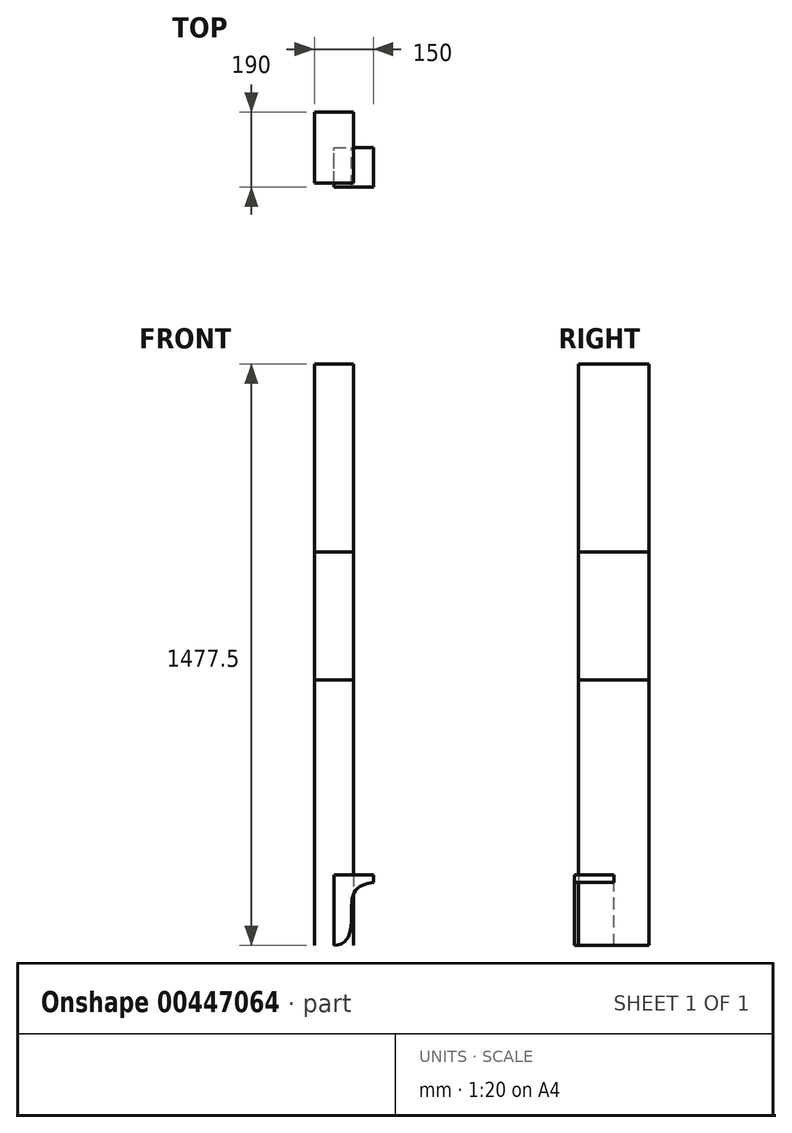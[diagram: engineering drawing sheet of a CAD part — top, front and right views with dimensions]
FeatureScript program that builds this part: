
annotation { "Feature Type Name" : "Feature", "Feature Type Description" : "" }
export const myFeature = defineFeature(function(context is Context, id is Id, definition is map)
    precondition{}
    {
        {
            var Q0;
            Q0=qCreatedBy(makeId("Top.planeOp"),FACE);
            var sketch = newSketch(context, id + "F0", { "sketchPlane" : qUnion([Q0])});
            skLineSegment(sketch, "E0.bottom", {"start": v(50, -90) * mm, "end": v(-50, -90) * mm});
            skLineSegment(sketch, "E0.top", {"start": v(50, 90) * mm, "end": v(-50, 90) * mm});
            skLineSegment(sketch, "E0.left", {"start": v(50, -90) * mm, "end": v(50, 90) * mm});
            skLineSegment(sketch, "E0.right", {"start": v(-50, -90) * mm, "end": v(-50, 90) * mm});
            skPoint(sketch, "E0.middle", {"position": v(0, 0) * mm});
            skSolve(sketch);
        }
        {
            var Q0;
            Q0=makeQuery(id+"F0.imprint","IMPRINT",FACE,{"disambiguationData":[TD([[makeQuery(id+"F0.imprint","IMPRINT",EDGE,{"derivedFrom":sQuery(id+"F0.wireOp",EDGE,"E0.bottom")}),-1.0]])]});
            extrude(context, id + "F1", {"entities" : qUnion([Q0]), "depth" : 1000 * mm, "offsetDistance" : 25 * mm});
        }
        {
            var Q0;
            Q0=makeQuery(id+"F0.imprint","IMPRINT",FACE,{"disambiguationData":[TD([[makeQuery(id+"F0.imprint","IMPRINT",EDGE,{"derivedFrom":sQuery(id+"F0.wireOp",EDGE,"E0.bottom")}),-1.0]])]});
            extrude(context, id + "F2", {"entities" : qUnion([Q0]), "depth" : 675 * mm, "offsetDistance" : 25 * mm});
        }
        {
            var Q0;
            Q0=makeQuery(id+"F0.imprint","IMPRINT",FACE,{"disambiguationData":[TD([[makeQuery(id+"F0.imprint","IMPRINT",EDGE,{"derivedFrom":sQuery(id+"F0.wireOp",EDGE,"E0.bottom")}),-1.0]])]});
            extrude(context, id + "F3", {"entities" : qUnion([Q0]), "depth" : 1477.5 * mm, "offsetDistance" : 25 * mm});
        }
        {
            var Q0;
            Q0=qCreatedBy(makeId("Front.planeOp"),FACE);
            var sketch = newSketch(context, id + "F4", { "sketchPlane" : qUnion([Q0])});
            skLineSegment(sketch, "E1", {"start": v(0, 0) * mm, "end": v(0, 180) * mm});
            skLineSegment(sketch, "E2", {"start": v(0, 180) * mm, "end": v(100, 180) * mm});
            skLineSegment(sketch, "E3", {"start": v(0, 0) * mm, "end": v(0, 0) * mm});
            skPoint(sketch, "E4.1.internal.snap0", {"position": v(0, 90) * mm});
            skFitSpline(sketch, "E5", {"points": [v(0, 0) * mm, v(45.1, 90) * mm, v(100, 160) * mm], "startDerivative": vector(262.5, 0) * mm, "endDerivative": vector(339.9, 45.16) * mm});
            skLineSegment(sketch, "E6", {"start": v(100, 180) * mm, "end": v(100, 160) * mm});
            skSolve(sketch);
        }
        {
            var Q0;
            Q0=makeQuery(id+"F4.imprint","IMPRINT",FACE,{"disambiguationData":[TD([[makeQuery(id+"F4.imprint","IMPRINT",EDGE,{"derivedFrom":sQuery(id+"F4.wireOp",EDGE,"E1")}),-1.0]])]});
            extrude(context, id + "F5", {"entities" : qUnion([Q0]), "depth" : 100 * mm, "offsetDistance" : 25 * mm});
        }
    });
